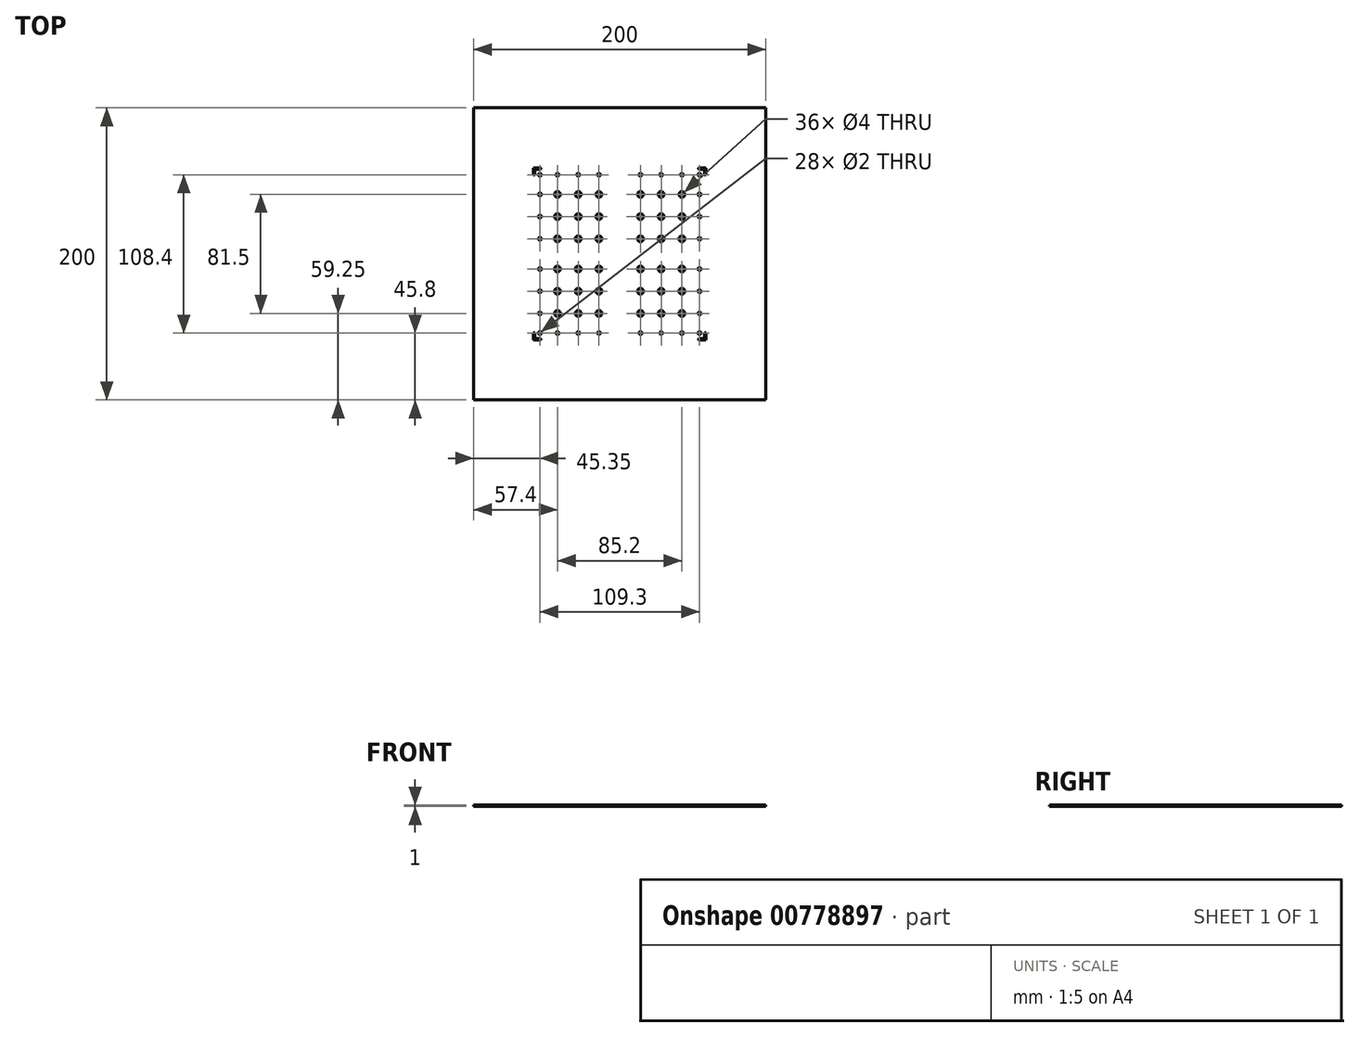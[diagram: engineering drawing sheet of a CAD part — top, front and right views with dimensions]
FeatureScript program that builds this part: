
annotation { "Feature Type Name" : "Feature", "Feature Type Description" : "" }
export const myFeature = defineFeature(function(context is Context, id is Id, definition is map)
    precondition{}
    {
        {
            var Q0;
            Q0=qCreatedBy(makeId("Top.planeOp"),FACE);
            var sketch = newSketch(context, id + "F0", { "sketchPlane" : qUnion([Q0])});
            skLineSegment(sketch, "E0.bottom", {"start": v(100, -100) * mm, "end": v(-100, -100) * mm});
            skLineSegment(sketch, "E0.top", {"start": v(100, 100) * mm, "end": v(-100, 100) * mm});
            skLineSegment(sketch, "E0.left", {"start": v(100, -100) * mm, "end": v(100, 100) * mm});
            skLineSegment(sketch, "E0.right", {"start": v(-100, -100) * mm, "end": v(-100, 100) * mm});
            skPoint(sketch, "E0.middle", {"position": v(0, 0) * mm});
            skSolve(sketch);
        }
        {
            var Q0;
            Q0=qSketchRegion(id+"F0",true);
            extrude(context, id + "F1", {"entities" : qUnion([Q0]), "depth" : 1 * mm, "offsetDistance" : 25 * mm});
        }
        {
            var Q0;
            Q0=makeQuery(id+"F1.opExtrude","CAP_FACE",FACE,{"disambiguationData":[OSD([sQuery(id+"F0.wireOp",EDGE,"E0.bottom"),sQuery(id+"F0.wireOp",EDGE,"E0.top"),sQuery(id+"F0.wireOp",EDGE,"E0.left"),sQuery(id+"F0.wireOp",EDGE,"E0.right")])],"isStart":false});
            var sketch = newSketch(context, id + "F2", { "sketchPlane" : qUnion([Q0])});
            skPoint(sketch, "E1", {"position": v(-42.6, 40.75) * mm});
            skPoint(sketch, "E2.0.1.0", {"position": v(-42.6, 25.55) * mm});
            skPoint(sketch, "E2.0.2.0", {"position": v(-42.6, 10.35) * mm});
            skPoint(sketch, "E2.1.0.0", {"position": v(-28.4, 40.75) * mm});
            skPoint(sketch, "E2.1.1.0", {"position": v(-28.4, 25.55) * mm});
            skPoint(sketch, "E2.1.2.0", {"position": v(-28.4, 10.35) * mm});
            skPoint(sketch, "E2.2.0.0", {"position": v(-14.2, 40.75) * mm});
            skPoint(sketch, "E2.2.1.0", {"position": v(-14.2, 25.55) * mm});
            skPoint(sketch, "E2.2.2.0", {"position": v(-14.2, 10.35) * mm});
            skPoint(sketch, "E2.3.0.0", {"position": v(0, 40.75) * mm});
            skPoint(sketch, "E2.3.1.0", {"position": v(0, 25.55) * mm});
            skPoint(sketch, "E2.3.2.0", {"position": v(0, 10.35) * mm});
            skPoint(sketch, "E2.4.0.0", {"position": v(14.2, 40.75) * mm});
            skPoint(sketch, "E2.4.1.0", {"position": v(14.2, 25.55) * mm});
            skPoint(sketch, "E2.4.2.0", {"position": v(14.2, 10.35) * mm});
            skPoint(sketch, "E2.5.0.0", {"position": v(28.4, 40.75) * mm});
            skPoint(sketch, "E2.5.1.0", {"position": v(28.4, 25.55) * mm});
            skPoint(sketch, "E2.5.2.0", {"position": v(28.4, 10.35) * mm});
            skPoint(sketch, "E2.6.0.0", {"position": v(42.6, 40.75) * mm});
            skPoint(sketch, "E2.6.1.0", {"position": v(42.6, 25.55) * mm});
            skPoint(sketch, "E2.6.2.0", {"position": v(42.6, 10.35) * mm});
            skLineSegment(sketch, "E2.direction1", {"start": v(-42.6, 40.75) * mm, "end": v(-28.4, 40.75) * mm, "construction": true});
            skLineSegment(sketch, "E2.direction2", {"start": v(-42.6, 40.75) * mm, "end": v(-42.6, 25.55) * mm, "construction": true});
            skLineSegment(sketch, "E3", {"start": v(0, 100) * mm, "end": v(0, -100) * mm, "construction": true});
            skLineSegment(sketch, "E4", {"start": v(-100, 0) * mm, "end": v(100, 0) * mm, "construction": true});
            skPoint(sketch, "E5.MirrorP", {"position": v(0, -40.75) * mm});
            skPoint(sketch, "E6.MirrorP", {"position": v(-42.6, -25.55) * mm});
            skLineSegment(sketch, "E7.MirrorCS", {"start": v(-42.6, -40.75) * mm, "end": v(-42.6, -25.55) * mm, "construction": true});
            skLineSegment(sketch, "E8.MirrorCS", {"start": v(-42.6, -40.75) * mm, "end": v(-28.4, -40.75) * mm, "construction": true});
            skPoint(sketch, "E9.MirrorP", {"position": v(-42.6, -10.35) * mm});
            skPoint(sketch, "E10.MirrorP", {"position": v(0, -25.55) * mm});
            skPoint(sketch, "E11.MirrorP", {"position": v(-28.4, -40.75) * mm});
            skPoint(sketch, "E12.MirrorP", {"position": v(28.4, -25.55) * mm});
            skPoint(sketch, "E13.MirrorP", {"position": v(28.4, -10.35) * mm});
            skPoint(sketch, "E14.MirrorP", {"position": v(-14.2, -25.55) * mm});
            skPoint(sketch, "E15.MirrorP", {"position": v(-42.6, -40.75) * mm});
            skPoint(sketch, "E16.MirrorP", {"position": v(14.2, -25.55) * mm});
            skPoint(sketch, "E17.MirrorP", {"position": v(28.4, -40.75) * mm});
            skPoint(sketch, "E18.MirrorP", {"position": v(-14.2, -40.75) * mm});
            skPoint(sketch, "E19.MirrorP", {"position": v(14.2, -10.35) * mm});
            skPoint(sketch, "E20.MirrorP", {"position": v(-14.2, -10.35) * mm});
            skPoint(sketch, "E21.MirrorP", {"position": v(42.6, -10.35) * mm});
            skPoint(sketch, "E22.MirrorP", {"position": v(0, -10.35) * mm});
            skPoint(sketch, "E23.MirrorP", {"position": v(14.2, -40.75) * mm});
            skPoint(sketch, "E24.MirrorP", {"position": v(42.6, -25.55) * mm});
            skPoint(sketch, "E25.MirrorP", {"position": v(-28.4, -10.35) * mm});
            skPoint(sketch, "E26.MirrorP", {"position": v(-28.4, -25.55) * mm});
            skPoint(sketch, "E27.MirrorP", {"position": v(42.6, -40.75) * mm});
            skLineSegment(sketch, "E28.bottom", {"start": v(58.12, -57.7) * mm, "end": v(-58.13, -57.7) * mm, "construction": true});
            skLineSegment(sketch, "E28.top", {"start": v(58.12, 57.7) * mm, "end": v(-58.12, 57.7) * mm, "construction": true});
            skLineSegment(sketch, "E28.left", {"start": v(58.12, -57.7) * mm, "end": v(58.12, 57.7) * mm, "construction": true});
            skLineSegment(sketch, "E28.right", {"start": v(-58.13, -57.7) * mm, "end": v(-58.12, 57.7) * mm, "construction": true});
            skPoint(sketch, "E28.middle", {"position": v(0, 0) * mm});
            skSolve(sketch);
        }
        {
            var Q0;
            Q0=sQuery(id+"F2.wireOp",VERTEX,"E1");
            var Q1;
            Q1=sQuery(id+"F2.wireOp",VERTEX,"E2.1.0.0");
            var Q2;
            Q2=sQuery(id+"F2.wireOp",VERTEX,"E2.2.0.0");
            var Q3;
            Q3=sQuery(id+"F2.wireOp",VERTEX,"E2.4.0.0");
            var Q4;
            Q4=sQuery(id+"F2.wireOp",VERTEX,"E2.5.0.0");
            var Q5;
            Q5=sQuery(id+"F2.wireOp",VERTEX,"E2.6.0.0");
            var Q6;
            Q6=sQuery(id+"F2.wireOp",VERTEX,"E2.0.1.0");
            var Q7;
            Q7=sQuery(id+"F2.wireOp",VERTEX,"E2.1.1.0");
            var Q8;
            Q8=sQuery(id+"F2.wireOp",VERTEX,"E2.2.1.0");
            var Q9;
            Q9=sQuery(id+"F2.wireOp",VERTEX,"E2.4.1.0");
            var Q10;
            Q10=sQuery(id+"F2.wireOp",VERTEX,"E2.5.1.0");
            var Q11;
            Q11=sQuery(id+"F2.wireOp",VERTEX,"E2.6.1.0");
            var Q12;
            Q12=sQuery(id+"F2.wireOp",VERTEX,"E2.6.2.0");
            var Q13;
            Q13=sQuery(id+"F2.wireOp",VERTEX,"E2.5.2.0");
            var Q14;
            Q14=sQuery(id+"F2.wireOp",VERTEX,"E2.4.2.0");
            var Q15;
            Q15=sQuery(id+"F2.wireOp",VERTEX,"E2.2.2.0");
            var Q16;
            Q16=sQuery(id+"F2.wireOp",VERTEX,"E2.1.2.0");
            var Q17;
            Q17=sQuery(id+"F2.wireOp",VERTEX,"E2.0.2.0");
            var Q18;
            Q18=sQuery(id+"F2.wireOp",VERTEX,"E9.MirrorP");
            var Q19;
            Q19=sQuery(id+"F2.wireOp",VERTEX,"E25.MirrorP");
            var Q20;
            Q20=sQuery(id+"F2.wireOp",VERTEX,"E20.MirrorP");
            var Q21;
            Q21=sQuery(id+"F2.wireOp",VERTEX,"E19.MirrorP");
            var Q22;
            Q22=sQuery(id+"F2.wireOp",VERTEX,"E13.MirrorP");
            var Q23;
            Q23=sQuery(id+"F2.wireOp",VERTEX,"E21.MirrorP");
            var Q24;
            Q24=sQuery(id+"F2.wireOp",VERTEX,"E24.MirrorP");
            var Q25;
            Q25=sQuery(id+"F2.wireOp",VERTEX,"E12.MirrorP");
            var Q26;
            Q26=sQuery(id+"F2.wireOp",VERTEX,"E16.MirrorP");
            var Q27;
            Q27=sQuery(id+"F2.wireOp",VERTEX,"E14.MirrorP");
            var Q28;
            Q28=sQuery(id+"F2.wireOp",VERTEX,"E26.MirrorP");
            var Q29;
            Q29=sQuery(id+"F2.wireOp",VERTEX,"E6.MirrorP");
            var Q30;
            Q30=sQuery(id+"F2.wireOp",VERTEX,"E15.MirrorP");
            var Q31;
            Q31=sQuery(id+"F2.wireOp",VERTEX,"E8.MirrorCS.end");
            var Q32;
            Q32=sQuery(id+"F2.wireOp",VERTEX,"E18.MirrorP");
            var Q33;
            Q33=sQuery(id+"F2.wireOp",VERTEX,"E23.MirrorP");
            var Q34;
            Q34=sQuery(id+"F2.wireOp",VERTEX,"E17.MirrorP");
            var Q35;
            Q35=sQuery(id+"F2.wireOp",VERTEX,"E27.MirrorP");
            var Q36;
            Q36=makeQuery(id+"F1.opExtrude","SWEPT_BODY",BODY,{"disambiguationData":[OSD([sQuery(id+"F0.wireOp",EDGE,"E0.bottom"),sQuery(id+"F0.wireOp",EDGE,"E0.top"),sQuery(id+"F0.wireOp",EDGE,"E0.left"),sQuery(id+"F0.wireOp",EDGE,"E0.right")])]});
            hole(context, id + "F3", {"style" : HoleStyle.SIMPLE, "endStyle" : HoleEndStyle.THROUGH, "standardTappedOrClearance" : lookupTablePath({ "standard" : "ISO", "size" : "4", "type" : "Drilled" }), "standardBlindInLast" : lookupTablePath({ "standard" : "ISO", "size" : "4", "type" : "Drilled" }), "holeDiameter" : 4 * mm, "majorDiameter" : 5 * mm, "isTappedThrough" : true, "tappedDepth" : 6.5 * mm, "tapClearance" : 3, "locations" : qUnion([Q0, Q1, Q2, Q3, Q4, Q5, Q6, Q7, Q8, Q9, Q10, Q11, Q12, Q13, Q14, Q15, Q16, Q17, Q18, Q19, Q20, Q21, Q22, Q23, Q24, Q25, Q26, Q27, Q28, Q29, Q30, Q31, Q32, Q33, Q34, Q35]), "scope" : qUnion([Q36])});
        }
        {
            var Q0;
            Q0=makeQuery(id+"F1.opExtrude","CAP_FACE",FACE,{"disambiguationData":[OSD([sQuery(id+"F0.wireOp",EDGE,"E0.bottom"),sQuery(id+"F0.wireOp",EDGE,"E0.top"),sQuery(id+"F0.wireOp",EDGE,"E0.left"),sQuery(id+"F0.wireOp",EDGE,"E0.right")])],"isStart":false});
            var sketch = newSketch(context, id + "F4", { "sketchPlane" : qUnion([Q0])});
            skLineSegment(sketch, "E29", {"start": v(-100, 0) * mm, "end": v(100, 0) * mm, "construction": true});
            skLineSegment(sketch, "E30", {"start": v(0, 100) * mm, "end": v(0, -100) * mm, "construction": true});
            skPoint(sketch, "E31", {"position": v(-54.65, 40.75) * mm});
            skPoint(sketch, "E32", {"position": v(-54.65, 25.55) * mm});
            skPoint(sketch, "E33", {"position": v(-54.65, 10.35) * mm});
            skPoint(sketch, "E34", {"position": v(-54.65, 54.2) * mm});
            skPoint(sketch, "E35", {"position": v(-42.6, 54.2) * mm});
            skPoint(sketch, "E36", {"position": v(-28.4, 54.2) * mm});
            skPoint(sketch, "E37", {"position": v(-14.2, 54.2) * mm});
            skPoint(sketch, "E38", {"position": v(0, 54.2) * mm});
            skPoint(sketch, "E39", {"position": v(14.2, 54.2) * mm});
            skPoint(sketch, "E40", {"position": v(28.4, 54.2) * mm});
            skPoint(sketch, "E41", {"position": v(42.6, 54.2) * mm});
            skPoint(sketch, "E42", {"position": v(54.65, 54.2) * mm});
            skPoint(sketch, "E43", {"position": v(54.65, 40.75) * mm});
            skPoint(sketch, "E44", {"position": v(54.65, 25.55) * mm});
            skPoint(sketch, "E45", {"position": v(54.65, 10.35) * mm});
            skLineSegment(sketch, "E46", {"start": v(-54.65, 54.2) * mm, "end": v(-42.6, 54.2) * mm, "construction": true});
            skLineSegment(sketch, "E47", {"start": v(42.6, 54.2) * mm, "end": v(54.65, 54.2) * mm, "construction": true});
            skPoint(sketch, "E48.MirrorP", {"position": v(54.65, -10.35) * mm});
            skPoint(sketch, "E49.MirrorP", {"position": v(54.65, -40.75) * mm});
            skPoint(sketch, "E50.MirrorP", {"position": v(54.65, -25.55) * mm});
            skPoint(sketch, "E51.MirrorP", {"position": v(-54.65, -10.35) * mm});
            skPoint(sketch, "E52.MirrorP", {"position": v(-54.65, -25.55) * mm});
            skPoint(sketch, "E53.MirrorP", {"position": v(-54.65, -40.75) * mm});
            skPoint(sketch, "E54.MirrorP", {"position": v(28.4, -54.2) * mm});
            skPoint(sketch, "E55.MirrorP", {"position": v(0, -54.2) * mm});
            skPoint(sketch, "E56.MirrorP", {"position": v(14.2, -54.2) * mm});
            skPoint(sketch, "E57.MirrorP", {"position": v(-14.2, -54.2) * mm});
            skPoint(sketch, "E58.MirrorP", {"position": v(-54.65, -54.2) * mm});
            skPoint(sketch, "E59.MirrorP", {"position": v(-42.6, -54.2) * mm});
            skPoint(sketch, "E60.MirrorP", {"position": v(-28.4, -54.2) * mm});
            skPoint(sketch, "E61.MirrorP", {"position": v(42.6, -54.2) * mm});
            skPoint(sketch, "E62.MirrorP", {"position": v(54.65, -54.2) * mm});
            skSolve(sketch);
        }
        {
            var Q0;
            Q0=sQuery(id+"F4.wireOp",VERTEX,"E34");
            var Q1;
            Q1=sQuery(id+"F4.wireOp",VERTEX,"E35");
            var Q2;
            Q2=sQuery(id+"F4.wireOp",VERTEX,"E36");
            var Q3;
            Q3=sQuery(id+"F4.wireOp",VERTEX,"E37");
            var Q4;
            Q4=sQuery(id+"F4.wireOp",VERTEX,"E39");
            var Q5;
            Q5=sQuery(id+"F4.wireOp",VERTEX,"E40");
            var Q6;
            Q6=sQuery(id+"F4.wireOp",VERTEX,"E41");
            var Q7;
            Q7=sQuery(id+"F4.wireOp",VERTEX,"E42");
            var Q8;
            Q8=sQuery(id+"F4.wireOp",VERTEX,"E43");
            var Q9;
            Q9=sQuery(id+"F4.wireOp",VERTEX,"E44");
            var Q10;
            Q10=sQuery(id+"F4.wireOp",VERTEX,"E45");
            var Q11;
            Q11=sQuery(id+"F4.wireOp",VERTEX,"E48.MirrorP");
            var Q12;
            Q12=sQuery(id+"F4.wireOp",VERTEX,"E50.MirrorP");
            var Q13;
            Q13=sQuery(id+"F4.wireOp",VERTEX,"E49.MirrorP");
            var Q14;
            Q14=sQuery(id+"F4.wireOp",VERTEX,"E62.MirrorP");
            var Q15;
            Q15=sQuery(id+"F4.wireOp",VERTEX,"E61.MirrorP");
            var Q16;
            Q16=sQuery(id+"F4.wireOp",VERTEX,"E54.MirrorP");
            var Q17;
            Q17=sQuery(id+"F4.wireOp",VERTEX,"E56.MirrorP");
            var Q18;
            Q18=sQuery(id+"F4.wireOp",VERTEX,"E57.MirrorP");
            var Q19;
            Q19=sQuery(id+"F4.wireOp",VERTEX,"E60.MirrorP");
            var Q20;
            Q20=sQuery(id+"F4.wireOp",VERTEX,"E59.MirrorP");
            var Q21;
            Q21=sQuery(id+"F4.wireOp",VERTEX,"E58.MirrorP");
            var Q22;
            Q22=sQuery(id+"F4.wireOp",VERTEX,"E53.MirrorP");
            var Q23;
            Q23=sQuery(id+"F4.wireOp",VERTEX,"E52.MirrorP");
            var Q24;
            Q24=sQuery(id+"F4.wireOp",VERTEX,"E51.MirrorP");
            var Q25;
            Q25=sQuery(id+"F4.wireOp",VERTEX,"E33");
            var Q26;
            Q26=sQuery(id+"F4.wireOp",VERTEX,"E32");
            var Q27;
            Q27=sQuery(id+"F4.wireOp",VERTEX,"E31");
            var Q28;
            Q28=makeQuery(id+"F1.opExtrude","SWEPT_BODY",BODY,{"disambiguationData":[OSD([sQuery(id+"F0.wireOp",EDGE,"E0.bottom"),sQuery(id+"F0.wireOp",EDGE,"E0.top"),sQuery(id+"F0.wireOp",EDGE,"E0.left"),sQuery(id+"F0.wireOp",EDGE,"E0.right")])]});
            hole(context, id + "F5", {"style" : HoleStyle.SIMPLE, "endStyle" : HoleEndStyle.THROUGH, "standardTappedOrClearance" : lookupTablePath({ "standard" : "ISO", "size" : "2", "type" : "Drilled" }), "standardBlindInLast" : lookupTablePath({ "standard" : "ISO", "size" : "2", "type" : "Drilled" }), "holeDiameter" : 2 * mm, "majorDiameter" : 5 * mm, "isTappedThrough" : true, "tappedDepth" : 6.5 * mm, "tapClearance" : 3, "locations" : qUnion([Q0, Q1, Q2, Q3, Q4, Q5, Q6, Q7, Q8, Q9, Q10, Q11, Q12, Q13, Q14, Q15, Q16, Q17, Q18, Q19, Q20, Q21, Q22, Q23, Q24, Q25, Q26, Q27]), "scope" : qUnion([Q28])});
        }
        {
            var Q0;
            Q0=makeQuery(id+"F1.opExtrude","CAP_FACE",FACE,{"disambiguationData":[OSD([sQuery(id+"F0.wireOp",EDGE,"E0.bottom"),sQuery(id+"F0.wireOp",EDGE,"E0.top"),sQuery(id+"F0.wireOp",EDGE,"E0.left"),sQuery(id+"F0.wireOp",EDGE,"E0.right")])],"isStart":false});
            var sketch = newSketch(context, id + "F6", { "sketchPlane" : qUnion([Q0])});
            skLineSegment(sketch, "E63.bottom", {"start": v(57.15, -57.15) * mm, "end": v(-57.15, -57.15) * mm, "construction": true});
            skLineSegment(sketch, "E63.top", {"start": v(57.15, 57.15) * mm, "end": v(-57.15, 57.15) * mm, "construction": true});
            skLineSegment(sketch, "E63.left", {"start": v(57.15, -57.15) * mm, "end": v(57.15, 57.15) * mm, "construction": true});
            skLineSegment(sketch, "E63.right", {"start": v(-57.15, -57.15) * mm, "end": v(-57.15, 57.15) * mm, "construction": true});
            skLineSegment(sketch, "E64.bottom", {"start": v(-59, 59) * mm, "end": v(-58, 59) * mm});
            skLineSegment(sketch, "E64.top", {"start": v(-59, 54) * mm, "end": v(-58, 54) * mm});
            skLineSegment(sketch, "E64.left", {"start": v(-59, 59) * mm, "end": v(-59, 54) * mm});
            skLineSegment(sketch, "E64.right", {"start": v(-58, 58) * mm, "end": v(-58, 54) * mm});
            skLineSegment(sketch, "E65.bottom", {"start": v(-59, 59) * mm, "end": v(-54, 59) * mm});
            skLineSegment(sketch, "E65.top", {"start": v(-58, 58) * mm, "end": v(-54, 58) * mm});
            skLineSegment(sketch, "E65.left", {"start": v(-59, 59) * mm, "end": v(-59, 58) * mm});
            skLineSegment(sketch, "E65.right", {"start": v(-54, 59) * mm, "end": v(-54, 58) * mm});
            skLineSegment(sketch, "E66", {"start": v(-57.15, 0) * mm, "end": v(57.15, 0) * mm, "construction": true});
            skLineSegment(sketch, "E67", {"start": v(0, 57.15) * mm, "end": v(0, -57.15) * mm, "construction": true});
            skPoint(sketch, "E68.center", {"position": v(0, 0) * mm});
            skLineSegment(sketch, "E69.1.0", {"start": v(-59, -59) * mm, "end": v(-59, -58) * mm});
            skLineSegment(sketch, "E69.1.1", {"start": v(-59, -59) * mm, "end": v(-54, -59) * mm});
            skLineSegment(sketch, "E69.1.2", {"start": v(-54, -59) * mm, "end": v(-54, -58) * mm});
            skLineSegment(sketch, "E69.1.3", {"start": v(-58, -58) * mm, "end": v(-54, -58) * mm});
            skLineSegment(sketch, "E69.1.4", {"start": v(-59, -59) * mm, "end": v(-58, -59) * mm});
            skLineSegment(sketch, "E69.1.5", {"start": v(-58, -58) * mm, "end": v(-58, -54) * mm});
            skLineSegment(sketch, "E69.1.6", {"start": v(-59, -54) * mm, "end": v(-58, -54) * mm});
            skLineSegment(sketch, "E69.1.7", {"start": v(-59, -59) * mm, "end": v(-59, -54) * mm});
            skLineSegment(sketch, "E69.2.0", {"start": v(59, -59) * mm, "end": v(58, -59) * mm});
            skLineSegment(sketch, "E69.2.1", {"start": v(59, -59) * mm, "end": v(59, -54) * mm});
            skLineSegment(sketch, "E69.2.2", {"start": v(59, -54) * mm, "end": v(58, -54) * mm});
            skLineSegment(sketch, "E69.2.3", {"start": v(58, -58) * mm, "end": v(58, -54) * mm});
            skLineSegment(sketch, "E69.2.4", {"start": v(59, -59) * mm, "end": v(59, -58) * mm});
            skLineSegment(sketch, "E69.2.5", {"start": v(58, -58) * mm, "end": v(54, -58) * mm});
            skLineSegment(sketch, "E69.2.6", {"start": v(54, -59) * mm, "end": v(54, -58) * mm});
            skLineSegment(sketch, "E69.2.7", {"start": v(59, -59) * mm, "end": v(54, -59) * mm});
            skLineSegment(sketch, "E69.3.0", {"start": v(59, 59) * mm, "end": v(59, 58) * mm});
            skLineSegment(sketch, "E69.3.1", {"start": v(59, 59) * mm, "end": v(54, 59) * mm});
            skLineSegment(sketch, "E69.3.2", {"start": v(54, 59) * mm, "end": v(54, 58) * mm});
            skLineSegment(sketch, "E69.3.3", {"start": v(58, 58) * mm, "end": v(54, 58) * mm});
            skLineSegment(sketch, "E69.3.4", {"start": v(59, 59) * mm, "end": v(58, 59) * mm});
            skLineSegment(sketch, "E69.3.5", {"start": v(58, 58) * mm, "end": v(58, 54) * mm});
            skLineSegment(sketch, "E69.3.6", {"start": v(59, 54) * mm, "end": v(58, 54) * mm});
            skLineSegment(sketch, "E69.3.7", {"start": v(59, 59) * mm, "end": v(59, 54) * mm});
            skSolve(sketch);
        }
        {
            var Q0;
            Q0 = qSketchRegion(id + "F6", true);
            extrude(context, id + "F7", {"entities" : qUnion([Q0]), "operationType" : NewBodyOperationType.REMOVE, "oppositeDirection" : true, "depth" : 0.1 * mm, "offsetDistance" : 25 * mm});
        }
        {
            var Q0;
            Q0=makeQuery(id+"F7.boolean.opBoolean","COPY",EDGE,{"derivedFrom":makeQuery(id+"F7.opExtrude","SWEPT_EDGE",EDGE,{"disambiguationData":[OSD([sQuery(id+"F6.wireOp",EDGE,"E65.bottom"),sQuery(id+"F6.wireOp",EDGE,"E65.right")])]})});
            var Q1;
            Q1=makeQuery(id+"F7.boolean.opBoolean","COPY",EDGE,{"derivedFrom":makeQuery(id+"F7.opExtrude","SWEPT_EDGE",EDGE,{"disambiguationData":[OSD([sQuery(id+"F6.wireOp",EDGE,"E65.top"),sQuery(id+"F6.wireOp",EDGE,"E65.right")])]})});
            var Q2;
            Q2=makeQuery(id+"F7.boolean.opBoolean","COPY",EDGE,{"derivedFrom":makeQuery(id+"F7.opExtrude","SWEPT_EDGE",EDGE,{"disambiguationData":[OSD([sQuery(id+"F6.wireOp",EDGE,"E65.bottom"),sQuery(id+"F6.wireOp",EDGE,"E65.left")])]})});
            var Q3;
            Q3=makeQuery(id+"F7.boolean.opBoolean","COPY",EDGE,{"derivedFrom":makeQuery(id+"F7.opExtrude","SWEPT_EDGE",EDGE,{"disambiguationData":[OSD([sQuery(id+"F6.wireOp",EDGE,"E64.top"),sQuery(id+"F6.wireOp",EDGE,"E64.left")])]})});
            var Q4;
            Q4=makeQuery(id+"F7.boolean.opBoolean","COPY",EDGE,{"derivedFrom":makeQuery(id+"F7.opExtrude","SWEPT_EDGE",EDGE,{"disambiguationData":[OSD([sQuery(id+"F6.wireOp",EDGE,"E64.top"),sQuery(id+"F6.wireOp",EDGE,"E64.right")])]})});
            var Q5;
            Q5=makeQuery(id+"F7.boolean.opBoolean","COPY",EDGE,{"derivedFrom":makeQuery(id+"F7.opExtrude","SWEPT_EDGE",EDGE,{"disambiguationData":[OSD([sQuery(id+"F6.wireOp",EDGE,"E69.3.1"),sQuery(id+"F6.wireOp",EDGE,"E69.3.2")])]})});
            var Q6;
            Q6=makeQuery(id+"F7.boolean.opBoolean","COPY",EDGE,{"derivedFrom":makeQuery(id+"F7.opExtrude","SWEPT_EDGE",EDGE,{"disambiguationData":[OSD([sQuery(id+"F6.wireOp",EDGE,"E69.3.2"),sQuery(id+"F6.wireOp",EDGE,"E69.3.3")])]})});
            var Q7;
            Q7=makeQuery(id+"F7.boolean.opBoolean","COPY",EDGE,{"derivedFrom":makeQuery(id+"F7.opExtrude","SWEPT_EDGE",EDGE,{"disambiguationData":[OSD([sQuery(id+"F6.wireOp",EDGE,"E69.3.4"),sQuery(id+"F6.wireOp",EDGE,"E69.3.7")])]})});
            var Q8;
            Q8=makeQuery(id+"F7.boolean.opBoolean","COPY",EDGE,{"derivedFrom":makeQuery(id+"F7.opExtrude","SWEPT_EDGE",EDGE,{"disambiguationData":[OSD([sQuery(id+"F6.wireOp",EDGE,"E69.3.6"),sQuery(id+"F6.wireOp",EDGE,"E69.3.7")])]})});
            var Q9;
            Q9=makeQuery(id+"F7.boolean.opBoolean","COPY",EDGE,{"derivedFrom":makeQuery(id+"F7.opExtrude","SWEPT_EDGE",EDGE,{"disambiguationData":[OSD([sQuery(id+"F6.wireOp",EDGE,"E69.3.5"),sQuery(id+"F6.wireOp",EDGE,"E69.3.6")])]})});
            var Q10;
            Q10=makeQuery(id+"F7.boolean.opBoolean","COPY",EDGE,{"derivedFrom":makeQuery(id+"F7.opExtrude","SWEPT_EDGE",EDGE,{"disambiguationData":[OSD([sQuery(id+"F6.wireOp",EDGE,"E69.2.1"),sQuery(id+"F6.wireOp",EDGE,"E69.2.2")])]})});
            var Q11;
            Q11=makeQuery(id+"F7.boolean.opBoolean","COPY",EDGE,{"derivedFrom":makeQuery(id+"F7.opExtrude","SWEPT_EDGE",EDGE,{"disambiguationData":[OSD([sQuery(id+"F6.wireOp",EDGE,"E69.2.2"),sQuery(id+"F6.wireOp",EDGE,"E69.2.3")])]})});
            var Q12;
            Q12=makeQuery(id+"F7.boolean.opBoolean","COPY",EDGE,{"derivedFrom":makeQuery(id+"F7.opExtrude","SWEPT_EDGE",EDGE,{"disambiguationData":[OSD([sQuery(id+"F6.wireOp",EDGE,"E69.2.4"),sQuery(id+"F6.wireOp",EDGE,"E69.2.7")])]})});
            var Q13;
            Q13=makeQuery(id+"F7.boolean.opBoolean","COPY",EDGE,{"derivedFrom":makeQuery(id+"F7.opExtrude","SWEPT_EDGE",EDGE,{"disambiguationData":[OSD([sQuery(id+"F6.wireOp",EDGE,"E69.2.5"),sQuery(id+"F6.wireOp",EDGE,"E69.2.6")])]})});
            var Q14;
            Q14=makeQuery(id+"F7.boolean.opBoolean","COPY",EDGE,{"derivedFrom":makeQuery(id+"F7.opExtrude","SWEPT_EDGE",EDGE,{"disambiguationData":[OSD([sQuery(id+"F6.wireOp",EDGE,"E69.2.6"),sQuery(id+"F6.wireOp",EDGE,"E69.2.7")])]})});
            var Q15;
            Q15=makeQuery(id+"F7.boolean.opBoolean","COPY",EDGE,{"derivedFrom":makeQuery(id+"F7.opExtrude","SWEPT_EDGE",EDGE,{"disambiguationData":[OSD([sQuery(id+"F6.wireOp",EDGE,"E69.1.5"),sQuery(id+"F6.wireOp",EDGE,"E69.1.6")])]})});
            var Q16;
            Q16=makeQuery(id+"F7.boolean.opBoolean","COPY",EDGE,{"derivedFrom":makeQuery(id+"F7.opExtrude","SWEPT_EDGE",EDGE,{"disambiguationData":[OSD([sQuery(id+"F6.wireOp",EDGE,"E69.1.6"),sQuery(id+"F6.wireOp",EDGE,"E69.1.7")])]})});
            var Q17;
            Q17=makeQuery(id+"F7.boolean.opBoolean","COPY",EDGE,{"derivedFrom":makeQuery(id+"F7.opExtrude","SWEPT_EDGE",EDGE,{"disambiguationData":[OSD([sQuery(id+"F6.wireOp",EDGE,"E69.1.4"),sQuery(id+"F6.wireOp",EDGE,"E69.1.7")])]})});
            var Q18;
            Q18=makeQuery(id+"F7.boolean.opBoolean","COPY",EDGE,{"derivedFrom":makeQuery(id+"F7.opExtrude","SWEPT_EDGE",EDGE,{"disambiguationData":[OSD([sQuery(id+"F6.wireOp",EDGE,"E69.1.2"),sQuery(id+"F6.wireOp",EDGE,"E69.1.3")])]})});
            var Q19;
            Q19=makeQuery(id+"F7.boolean.opBoolean","COPY",EDGE,{"derivedFrom":makeQuery(id+"F7.opExtrude","SWEPT_EDGE",EDGE,{"disambiguationData":[OSD([sQuery(id+"F6.wireOp",EDGE,"E69.1.1"),sQuery(id+"F6.wireOp",EDGE,"E69.1.2")])]})});
            fillet(context, id + "F8", {"entities" : qUnion([Q0, Q1, Q2, Q3, Q4, Q5, Q6, Q7, Q8, Q9, Q10, Q11, Q12, Q13, Q14, Q15, Q16, Q17, Q18, Q19]), "radius" : 0.5 * mm, "tangentPropagation" : true, "allowEdgeOverflow" : false});
        }
    });
